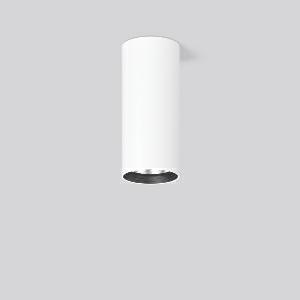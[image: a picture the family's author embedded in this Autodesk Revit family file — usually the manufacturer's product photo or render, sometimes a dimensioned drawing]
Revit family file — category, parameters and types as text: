
# Revit family: heledon_mini_a_931202_002_1_76_2687
name_source: partatom
category: Lighting Fixtures
units: mm (PartAtom-declared; Revit-internal decimal feet)

## family parameters
Cut with Voids When Loaded = No
Host = Face
Light Source = No
Part Type = Normal
Room Calculation Point = No
Round Connector Dimension = Use Diameter
Shared = No

## types (1)
- HELEDON mini A (1 x LED Modul 940, 2750 lm, 4000)
    Apparent Load = 20 VA
    Approval mark = CE
    CIE Flux Codes = 95 99 100 100 100
    Color Rendering = 92
    Color Temperature = 4000
    Default Elevation = 1800 mm
    Description = Series: HELEDON mini
Cylindrical surface-mounted downlight. Housing: die-cast aluminium, powder-coated. Internal ceiling frame polycarbonate with bayonet mounting. Black plastic ring and recessed LED to prevent glare from the side. Optical assembly with reflector made of MIRO-Silver with 98% total light reflection for outstanding efficiency - can be changed without tools. Best colour rendering index Ra>90. Suitable for Ceiling mounting. Easy installation with a separate ceiling frame with bayonet mounting and plug connection. Driver integrated. Connected via plug-in connector. High quality converter without flickering and stroboscopic effect. The following accessories can be mounted without use of tools: interchangeable lenses, decorative glasses, honeycomb louvre, clear and frosted diffusers, white interchangeable plastic ring. 
Colour: traffic white, matt (RAL 9016)
Diameter: 87 mm
Height: 197 mm
Lamp: LED
Socket: without socket
Colour temperature: 4000K
Colour rendering index (CRI): 92
System power: 20 W
Rated luminous flux: 2750 lm
Luminous efficiency: 138 lm/W
Control gear: Converter, dimmable, DALI
Protection class: I
Type of protection: IP 20
    Height = 197 mm
    Lamp = 1 x LED Modul 940
    Lamp Light Flux = 2750 lm
    Lamp count = 1
    Length = 87 mm
    Lifetime = 50000 h
    Luminous efficacy = 138 lm/W
    Manufacturer = RZB
    ModVariant = No
    Model = 931202.002.1.76
    Mounting Place = Ceiling
    Mounting Type = Surface mounted
    Number of Poles = 1
    OnlyDefault = Yes
    Power Factor = 1
    Product Name = HELEDON mini A
    Product group = Surface mounted downlights
    ProductGroupID = 302
    Protection Class = Protection class I
    Protection Degree = IP 20
    RLX_Detail_Level = 1
    RLX_Emergency_Light_Flux = 0 lm
    RLX_Emergency_Type = 0
    RLX_Emergency_Type_DB = No
    RlxData = <blob elided: 107293 chars, md5=c753642a>
    Socket = socket
    Standby Power = 0 W
    System Light Flux = 2750 lm
    System Power = 20 W
    Type Comments = Product without accessories
    Type Image = 931188.002.jpg
    URL = http://relux.com
    VarID = ---
    Voltage = 230 V
    Voltage Range = 220-240 V
    Weight = 0.00 kg
    Width = 0 mm  [stored 0 ft]

note: [stored X ft] marks values corroborated as IEEE doubles in the binary element streams (Revit-internal decimal feet)

## geometry (parser evidence)
native form markers: Blend x4, Sweep x8
no freeform markers — native parametric forms only
